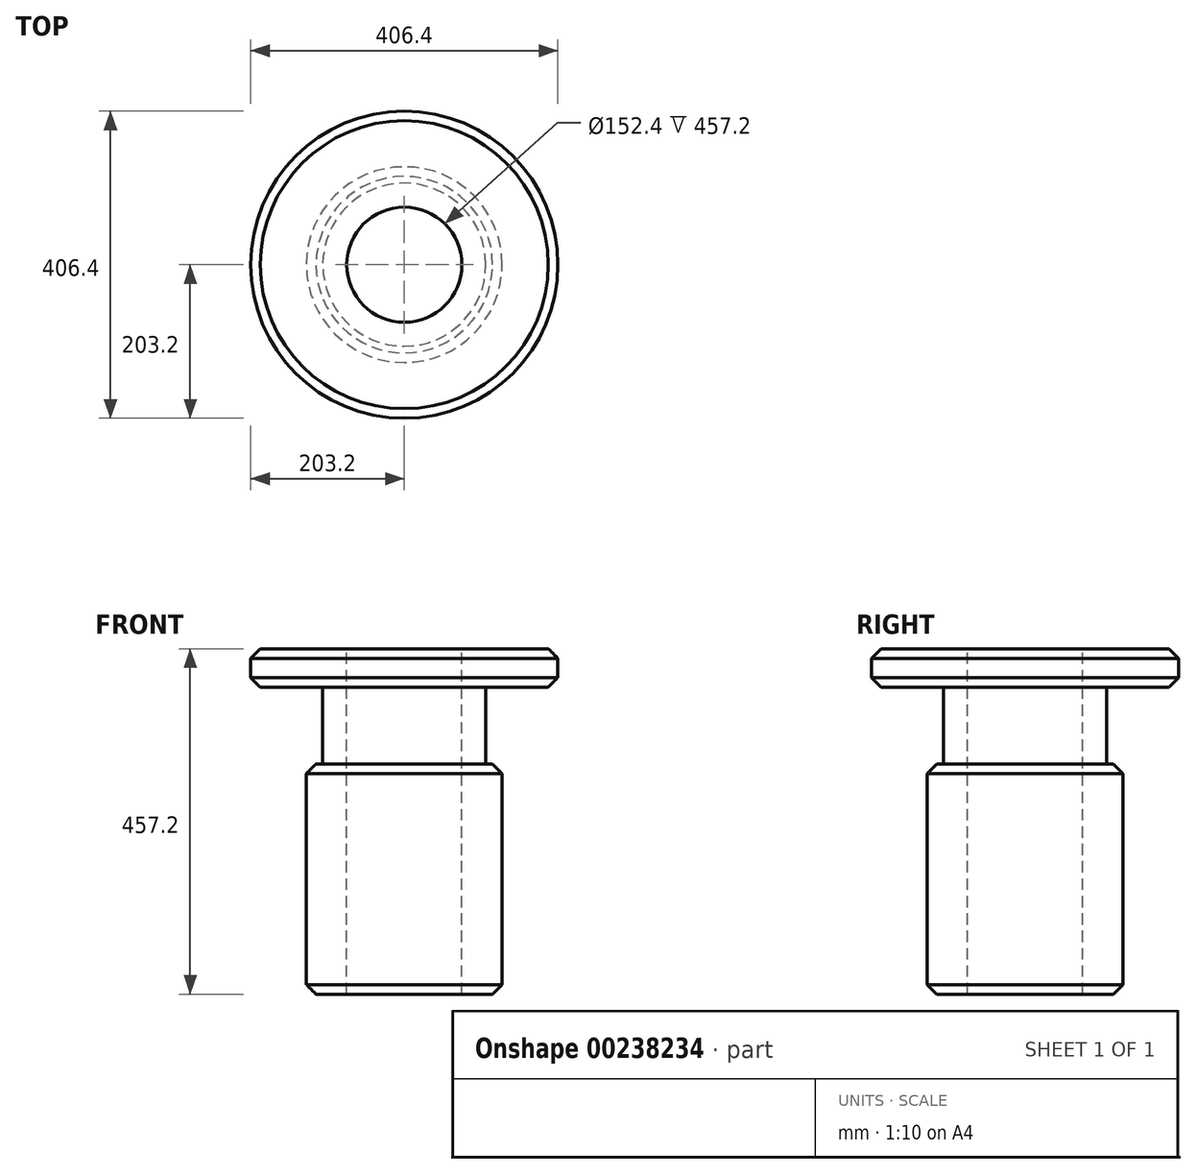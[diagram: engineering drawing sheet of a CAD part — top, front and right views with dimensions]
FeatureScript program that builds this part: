
annotation { "Feature Type Name" : "Feature", "Feature Type Description" : "" }
export const myFeature = defineFeature(function(context is Context, id is Id, definition is map)
    precondition{}
    {
        {
            var Q0;
            Q0=qCreatedBy(makeId("Top.planeOp"),FACE);
            var sketch = newSketch(context, id + "F0", { "sketchPlane" : qUnion([Q0])});
            skCircle(sketch, "E0", {"center": v(0, 0) * mm, "radius": 203.2 * mm});
            skSolve(sketch);
        }
        {
            var Q0;
            Q0 = qSketchRegion(id + "F0", true);
            extrude(context, id + "F1", {"entities" : qUnion([Q0]), "depth" : 50.8 * mm});
        }
        {
            var Q0;
            Q0=makeQuery(id+"F1.opExtrude","CAP_FACE",FACE,{"disambiguationData":[OSD([sQuery(id+"F0.wireOp",EDGE,"E0")])],"isStart":true});
            var sketch = newSketch(context, id + "F2", { "sketchPlane" : qUnion([Q0])});
            skCircle(sketch, "E1", {"center": v(0, 0) * mm, "radius": 107.95 * mm});
            skSolve(sketch);
        }
        {
            var Q0;
            Q0 = qSketchRegion(id + "F2", true);
            extrude(context, id + "F3", {"entities" : qUnion([Q0]), "operationType" : NewBodyOperationType.ADD, "depth" : 101.6 * mm});
        }
        {
            var Q0;
            Q0=makeQuery(id+"F3.opExtrude","CAP_FACE",FACE,{"disambiguationData":[OSD([sQuery(id+"F2.wireOp",EDGE,"E1")])],"isStart":false});
            var sketch = newSketch(context, id + "F4", { "sketchPlane" : qUnion([Q0])});
            skCircle(sketch, "E2", {"center": v(0, 0) * mm, "radius": 129.54 * mm});
            skSolve(sketch);
        }
        {
            var Q0;
            Q0 = qSketchRegion(id + "F4", true);
            extrude(context, id + "F5", {"entities" : qUnion([Q0]), "operationType" : NewBodyOperationType.ADD, "depth" : 304.8 * mm});
        }
        {
            var Q0;
            Q0=makeQuery(id+"F1.opExtrude","CAP_FACE",FACE,{"disambiguationData":[OSD([sQuery(id+"F0.wireOp",EDGE,"E0")])],"isStart":false});
            var sketch = newSketch(context, id + "F6", { "sketchPlane" : qUnion([Q0])});
            skCircle(sketch, "E3", {"center": v(0, 0) * mm, "radius": 76.2 * mm});
            skSolve(sketch);
        }
        {
            var Q0;
            Q0 = qSketchRegion(id + "F6", true);
            extrude(context, id + "F7", {"entities" : qUnion([Q0]), "operationType" : NewBodyOperationType.REMOVE, "oppositeDirection" : true, "depth" : 457.2 * mm});
        }
        {
            var Q0;
            Q0=makeQuery(id+"F1.opExtrude","CAP_EDGE",EDGE,{"disambiguationData":[OSD([sQuery(id+"F0.wireOp",EDGE,"E0")])],"isStart":false});
            chamfer(context, id + "F8", {"entities" : qUnion([Q0]), "width" : 12.7 * mm, "tangentPropagation" : true});
        }
        {
            var Q0;
            Q0=makeQuery(id+"F1.opExtrude","CAP_EDGE",EDGE,{"disambiguationData":[OSD([sQuery(id+"F0.wireOp",EDGE,"E0")])],"isStart":true});
            chamfer(context, id + "F9", {"entities" : qUnion([Q0]), "width" : 12.7 * mm, "tangentPropagation" : true});
        }
        {
            var Q0;
            Q0=makeQuery(id+"F5.opExtrude","CAP_EDGE",EDGE,{"disambiguationData":[OSD([sQuery(id+"F4.wireOp",EDGE,"E2")])],"isStart":true});
            var Q1;
            Q1=makeQuery(id+"F5.opExtrude","CAP_EDGE",EDGE,{"disambiguationData":[OSD([sQuery(id+"F4.wireOp",EDGE,"E2")])],"isStart":false});
            chamfer(context, id + "F10", {"entities" : qUnion([Q0, Q1]), "width" : 12.7 * mm, "tangentPropagation" : true});
        }
    });
